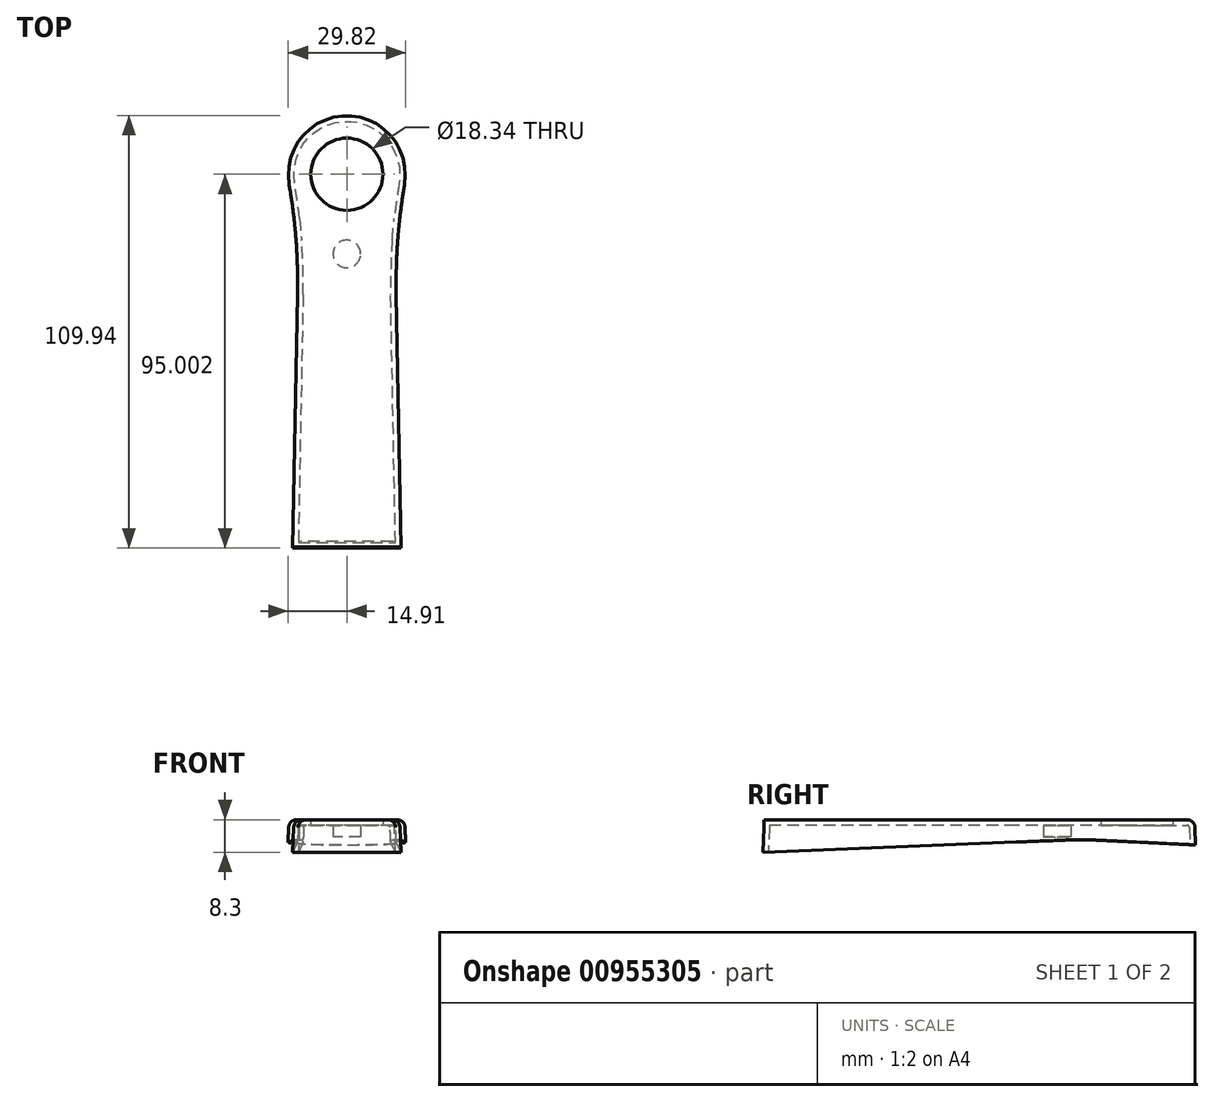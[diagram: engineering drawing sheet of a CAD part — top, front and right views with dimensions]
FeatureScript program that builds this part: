
annotation { "Feature Type Name" : "Feature", "Feature Type Description" : "" }
export const myFeature = defineFeature(function(context is Context, id is Id, definition is map)
    precondition{}
    {
        {
            var Q0;
            Q0=qCreatedBy(makeId("Top.planeOp"),FACE);
            var sketch = newSketch(context, id + "F0", { "sketchPlane" : qUnion([Q0])});
            skCircle(sketch, "E0", {"center": v(0, 42.9) * mm, "radius": 15 * mm});
            skLineSegment(sketch, "E1", {"start": v(-12.25, 34.25) * mm, "end": v(-13.75, -52.1) * mm});
            skLineSegment(sketch, "E2.MirrorCS", {"start": v(13.75, -52.1) * mm, "end": v(0, -52.37) * mm});
            skLineSegment(sketch, "E3.MirrorCS", {"start": v(12.25, 34.25) * mm, "end": v(13.75, -52.1) * mm});
            skLineSegment(sketch, "E4", {"start": v(-22.96, -39.9) * mm, "end": v(24.26, -39.9) * mm, "construction": true});
            skLineSegment(sketch, "E5", {"start": v(-22.63, 27.9) * mm, "end": v(23.45, 27.9) * mm, "construction": true});
            skLineSegment(sketch, "E6", {"start": v(-22.5, 57.9) * mm, "end": v(23.03, 57.9) * mm, "construction": true});
            skLineSegment(sketch, "E7", {"start": v(-13.75, -52.1) * mm, "end": v(13.75, -52.1) * mm});
            skSolve(sketch);
        }
        {
            var Q0;
            {var subQ0=sQuery(id+"F0.wireOp",EDGE,"E1");Q0=makeQuery(id+"F0.imprint","IMPRINT",FACE,{"disambiguationData":[TD([[makeQuery(id+"F0.imprint","IMPRINT",EDGE,{"derivedFrom":subQ0}),1.0]])]});}
            var Q1;
            {var subQ0=sQuery(id+"F0.wireOp",EDGE,"E0");var subQ1=makeQuery(id+"F0.imprint","INTERSECT",VERTEX,{"derivedFrom":[subQ0,sQuery(id+"F0.wireOp",EDGE,"E1")]});Q1=makeQuery(id+"F0.imprint","IMPRINT",FACE,{"disambiguationData":[TD([[makeQuery(id+"F0.imprint","IMPRINT",EDGE,{"disambiguationData":[TD([[subQ1,-1.0]])],"derivedFrom":subQ0}),1.0]])]});}
            extrude(context, id + "F1", {"entities" : qUnion([Q0, Q1]), "depth" : 8.3 * mm, "offsetDistance" : 25 * mm, "hasDraft" : true, "draftAngle" : 2 * degree, "draftPullDirection" : true});
        }
        {
            var Q0;
            Q0=makeQuery(id+"F1.opExtrude","SWEPT_EDGE",EDGE,{"disambiguationData":[OSD([sQuery(id+"F0.wireOp",EDGE,"E0"),sQuery(id+"F0.wireOp",EDGE,"E1")])]});
            var Q1;
            Q1=makeQuery(id+"F1.opExtrude","SWEPT_EDGE",EDGE,{"disambiguationData":[OSD([sQuery(id+"F0.wireOp",EDGE,"E0"),sQuery(id+"F0.wireOp",EDGE,"E3.MirrorCS")])]});
            fillet(context, id + "F2", {"entities" : qUnion([Q0, Q1]), "radius" : 150 * mm, "tangentPropagation" : true, "allowEdgeOverflow" : false});
        }
        {
            var Q0;
            Q0=makeQuery(id+"F1.opExtrude","CAP_EDGE",EDGE,{"disambiguationData":[OSD([sQuery(id+"F0.wireOp",EDGE,"E1")])],"isStart":false});
            fillet(context, id + "F3", {"entities" : qUnion([Q0]), "radius" : 2 * mm, "tangentPropagation" : true, "allowEdgeOverflow" : false});
        }
        {
            var Q0;
            Q0=makeQuery(id+"F1.opExtrude","CAP_FACE",FACE,{"disambiguationData":[OSD([sQuery(id+"F0.wireOp",EDGE,"E0"),sQuery(id+"F0.wireOp",EDGE,"E1"),sQuery(id+"F0.wireOp",EDGE,"UaFMypc2-69WY-RVk6-lVYq-pUJX6FrObcbF"),sQuery(id+"F0.wireOp",EDGE,"E2.MirrorCS"),sQuery(id+"F0.wireOp",EDGE,"E3.MirrorCS")])],"isStart":true});
            shell(context, id + "F4", {"entities" : qUnion([Q0]), "thickness" : 1.4 * mm});
        }
        {
            var Q0;
            {var subQ0=sQuery(id+"F0.wireOp",EDGE,"E7");var subQ1=sQuery(id+"F0.wireOp",EDGE,"E3.MirrorCS");var subQ2=sQuery(id+"F0.wireOp",EDGE,"E1");var subQ3=sQuery(id+"F0.wireOp",EDGE,"E0");Q0=makeQuery(id+"F4.opShell","OFFSET_FACE",FACE,{"disambiguationData":[OSD([subQ3,subQ2,subQ1,subQ0]),TDD([makeQuery(id+"F1.opExtrude","CAP_FACE",FACE,{"disambiguationData":[OSD([subQ3,subQ2,subQ1,subQ0])],"isStart":false})])]});}
            var sketch = newSketch(context, id + "F5", { "sketchPlane" : qUnion([Q0])});
            skCircle(sketch, "E8", {"center": v(0, -42.9) * mm, "radius": 9.17 * mm});
            skSolve(sketch);
        }
        {
            var Q0;
            Q0 = qSketchRegion(id + "F5", true);
            extrude(context, id + "F6", {"entities" : qUnion([Q0]), "operationType" : NewBodyOperationType.REMOVE, "oppositeDirection" : true, "depth" : 25 * mm, "offsetDistance" : 25 * mm});
        }
        {
            var Q0;
            {var subQ0=sQuery(id+"F0.wireOp",EDGE,"E1");Q0=makeQuery(id+"F0.imprint","IMPRINT",FACE,{"disambiguationData":[TD([[makeQuery(id+"F0.imprint","IMPRINT",EDGE,{"derivedFrom":subQ0}),1.0]])]});}
            var sketch = newSketch(context, id + "F7", { "sketchPlane" : qUnion([Q0])});
            skCircle(sketch, "E9", {"center": v(0, 22.66) * mm, "radius": 3.5 * mm});
            skSolve(sketch);
        }
        {
            var Q0;
            Q0=makeQuery(id+"F7.imprint","IMPRINT",FACE,{"disambiguationData":[TD([[makeQuery(id+"F7.imprint","IMPRINT",EDGE,{"derivedFrom":sQuery(id+"F7.wireOp",EDGE,"E9")}),1.0]])]});
            var Q1;
            {var subQ0=sQuery(id+"F0.wireOp",EDGE,"E7");var subQ1=sQuery(id+"F0.wireOp",EDGE,"E3.MirrorCS");var subQ2=sQuery(id+"F0.wireOp",EDGE,"E1");var subQ3=sQuery(id+"F0.wireOp",EDGE,"E0");Q1=makeQuery(id+"F4.opShell","OFFSET_FACE",FACE,{"disambiguationData":[OSD([subQ3,subQ2,subQ1,subQ0]),TDD([makeQuery(id+"F1.opExtrude","CAP_FACE",FACE,{"disambiguationData":[OSD([subQ3,subQ2,subQ1,subQ0])],"isStart":false})])]});}
            extrude(context, id + "F8", {"entities" : qUnion([Q0]), "operationType" : NewBodyOperationType.ADD, "endBound" : BoundingType.UP_TO_SURFACE, "depth" : 25 * mm, "endBoundEntityFace" : qUnion([Q1]), "offsetDistance" : 25 * mm});
        }
        {
            var Q0;
            Q0=makeQuery(id+"F8.opExtrude","CAP_FACE",FACE,{"disambiguationData":[OSD([sQuery(id+"F7.wireOp",EDGE,"E9")])],"isStart":true});
            extrude(context, id + "F9", {"entities" : qUnion([Q0]), "operationType" : NewBodyOperationType.REMOVE, "oppositeDirection" : true, "depth" : 4 * mm, "offsetDistance" : 25 * mm});
        }
        {
            var Q0;
            Q0=qCreatedBy(makeId("Right.planeOp"),FACE);
            var sketch = newSketch(context, id + "F10", { "sketchPlane" : qUnion([Q0])});
            skLineSegment(sketch, "E10", {"start": v(57.9, 1.9) * mm, "end": v(28.94, 3.3) * mm});
            skLineSegment(sketch, "E11", {"start": v(28.94, 3.3) * mm, "end": v(-52.1, 0) * mm});
            skLineSegment(sketch, "E12", {"start": v(57.9, 1.9) * mm, "end": v(57.9, 0) * mm});
            skLineSegment(sketch, "E13", {"start": v(57.9, 0) * mm, "end": v(-52.1, 0) * mm});
            skSolve(sketch);
        }
        {
            var Q0;
            Q0 = qSketchRegion(id + "F10", true);
            extrude(context, id + "F11", {"entities" : qUnion([Q0]), "depth" : 25 * mm, "offsetDistance" : 25 * mm, "hasSecondDirection" : true, "secondDirectionOppositeDirection" : true, "secondDirectionDepth" : 25 * mm});
        }
        {
            var Q0;
            Q0=makeQuery(id+"F11.opExtrude","SWEPT_EDGE",EDGE,{"disambiguationData":[OSD([sQuery(id+"F10.wireOp",EDGE,"E10"),sQuery(id+"F10.wireOp",EDGE,"E11")])]});
            fillet(context, id + "F12", {"entities" : qUnion([Q0]), "radius" : 60 * mm, "tangentPropagation" : true, "allowEdgeOverflow" : false});
        }
        {
            var Q0;
            Q0=makeQuery(id+"F11.opExtrude","SWEPT_BODY",BODY,{"disambiguationData":[OSD([sQuery(id+"F10.wireOp",EDGE,"E10"),sQuery(id+"F10.wireOp",EDGE,"E11"),sQuery(id+"F10.wireOp",EDGE,"E12"),sQuery(id+"F10.wireOp",EDGE,"E13")])]});
            var Q1;
            Q1=makeQuery(id+"F1.opExtrude","SWEPT_BODY",BODY,{"disambiguationData":[OSD([sQuery(id+"F0.wireOp",EDGE,"E0"),sQuery(id+"F0.wireOp",EDGE,"E1"),sQuery(id+"F0.wireOp",EDGE,"E3.MirrorCS"),sQuery(id+"F0.wireOp",EDGE,"E7")])]});
            booleanBodies(context, id + "F13", {"operationType" : BooleanOperationType.SUBTRACTION, "tools" : qUnion([Q0]), "targets" : qUnion([Q1])});
        }
    });
